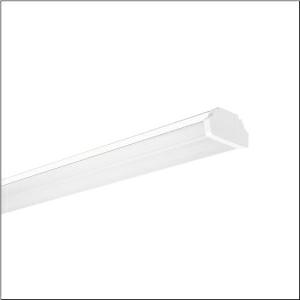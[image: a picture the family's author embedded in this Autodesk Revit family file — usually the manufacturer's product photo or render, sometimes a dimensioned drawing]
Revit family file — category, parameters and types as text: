
# Revit family: dus_31_gen_2_53bd812dv4a5c2_ed1e
name_source: partatom
category: Lighting Fixtures
units: mm (PartAtom-declared; Revit-internal decimal feet)

## family parameters
Cut with Voids When Loaded = No
Host = Face
Light Source = No
Part Type = Normal
Room Calculation Point = No
Round Connector Dimension = Use Diameter
Shared = No

## types (1)
- --- (1 x LED, 10860 lm, 61.4 W, 4000K)
    Apparent Load = 61 VA
    CIE Flux Codes = 47 80 95 93 100
    Color Rendering = 80
    Color Temperature = 4000K
    Default Elevation = 1800 mm
    Description = DUS 31 Gen.2, luminaire insert, of sheet steel, coil coated, white, length: 1.535mm, width: 81mm, height: 90mm, 5x system unit, system units: 307mm, LED rated luminous flux: 10.860lm, light colour: 840, SDCM (Standard Deviation of Colour Matching)MacAdam ≤ 3 SDCM (initial), control gear: DALI 2, control gear: ECG DALI, with plug, 5-pole, with phase selection, mains connection: 220..240V, AC, 50/60Hz, rated input power: 61W, through-wiring accessed according to module size, primary optical cover: cover, of PMMA, light emission: direct distribution, primary light characteristic: symmetric, protection rating (complete): IP20, protection rating (LED compartment): IP50, insulation class (complete): insulation class I (protective earthing), certification: CE, ENEC, VDE, UKCA, impact resistance: IK03, permissible ambient temperature for indoor applications: -25..+35°C, corresponds to IFS (International Featured Standards) requirements for safety and quality in the food industry, reducing of maximum allowable ambient temperature of 5°C with ceiling mounting, packaging unit: 1 piece
    Height = 95 mm
    Lamp = 1 x LED
    Lamp Light Flux = 10860 lm
    Lamp Power = 61.4 W
    Lamp count = 1
    Length = 1535 mm
    Luminous efficacy = 177 lm/W
    Manufacturer = Siteco
    ModVariant = No
    Model = 53BD812DV4A5C2
    Mounting Place = Ceiling
    Mounting Type = Pendant
    Number of Poles = 1
    OnlyDefault = Yes
    Power Factor = 1
    Product Name = DUS 31 Gen.2
    Product group = luminaire insert | ceiling pendant
    ProductGroupID = 901
    Protection Class = Protection class I
    Protection Degree = IP 20
    RLX_Detail_Level = 1
    RLX_Emergency_Light_Flux = 0 lm
    RLX_Emergency_Type = 0
    RLX_Emergency_Type_DB = No
    RlxData = <blob elided: 32141 chars, md5=10f36c2d>
    Socket = socket
    Standby Power = 0 W
    System Light Flux = 10860 lm
    System Power = 61 W
    Type Comments = factory setting: luminous flux: 100 % | dim-lin: 254 | 418 mA
    Type Image = l_1319596.jpg
    URL = http://relux.com
    VarID = @adj_051389
    Voltage = 0 V
    Weight = 0.00 kg
    Width = 81 mm

## geometry (parser evidence)
native form markers: Blend x4, Sweep x13
no freeform markers — native parametric forms only
